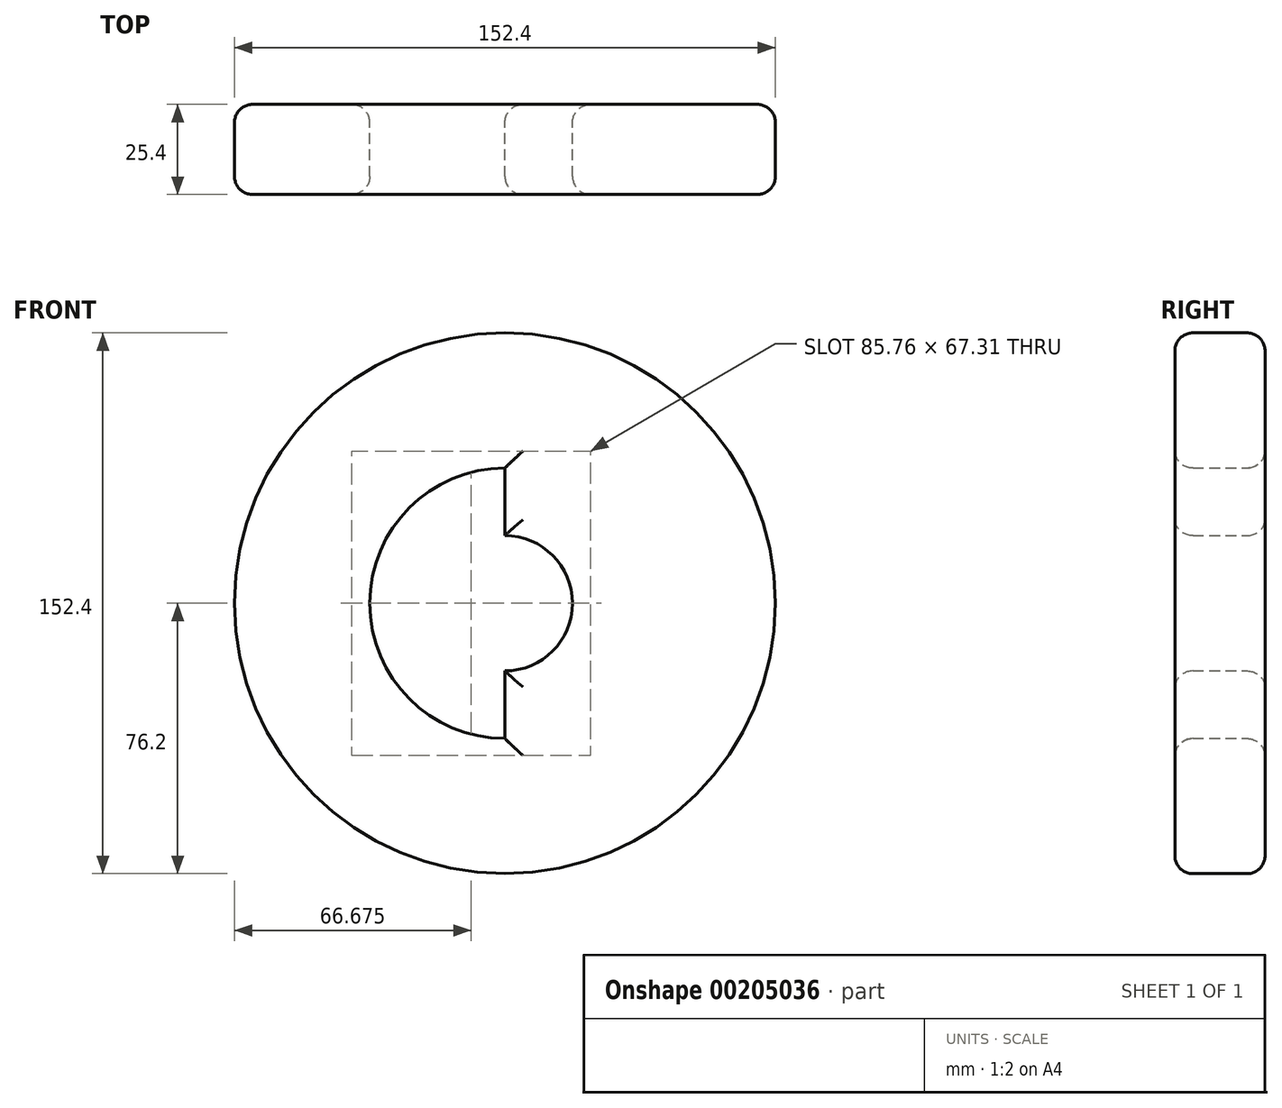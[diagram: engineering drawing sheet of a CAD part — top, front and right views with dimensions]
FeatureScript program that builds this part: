
annotation { "Feature Type Name" : "Feature", "Feature Type Description" : "" }
export const myFeature = defineFeature(function(context is Context, id is Id, definition is map)
    precondition{}
    {
        {
            var Q0;
            Q0=qCreatedBy(makeId("Front.planeOp"),FACE);
            var sketch = newSketch(context, id + "F0", { "sketchPlane" : qUnion([Q0])});
            skCircle(sketch, "E0", {"center": v(0, 0) * mm, "radius": 76.2 * mm});
            skLineSegment(sketch, "E1", {"start": v(-76.2, 0) * mm, "end": v(76.2, 0) * mm});
            skLineSegment(sketch, "E2", {"start": v(0, 76.2) * mm, "end": v(0, -76.2) * mm});
            skCircle(sketch, "E3", {"center": v(0, 0) * mm, "radius": 38.1 * mm});
            skSolve(sketch);
        }
        {
            var Q0;
            Q0=makeQuery(id+"F0.imprint","IMPRINT",FACE,{"disambiguationData":[TD([[makeQuery(id+"F0.imprint","IMPRINT",EDGE,{"derivedFrom":sQuery(id+"F0.wireOp",EDGE,"E0")}),1.0]])]});
            var Q1;
            {var subQ0=sQuery(id+"F0.wireOp",EDGE,"E3");var subQ1=sQuery(id+"F0.wireOp",EDGE,"E1");var subQ2=makeQuery(id+"F0.imprint","INTERSECT",VERTEX,{"disambiguationData":[OD(0.0)],"derivedFrom":[subQ1,subQ0]});Q1=makeQuery(id+"F0.imprint","IMPRINT",FACE,{"disambiguationData":[TD([[makeQuery(id+"F0.imprint","IMPRINT",EDGE,{"disambiguationData":[TD([[subQ2,-1.0]])],"derivedFrom":subQ1}),1.0]])]});}
            var Q2;
            {var subQ0=sQuery(id+"F0.wireOp",EDGE,"E3");var subQ1=sQuery(id+"F0.wireOp",EDGE,"E1");var subQ2=makeQuery(id+"F0.imprint","INTERSECT",VERTEX,{"disambiguationData":[OD(0.0)],"derivedFrom":[subQ1,subQ0]});Q2=makeQuery(id+"F0.imprint","IMPRINT",FACE,{"disambiguationData":[TD([[makeQuery(id+"F0.imprint","IMPRINT",EDGE,{"disambiguationData":[TD([[subQ2,-1.0]])],"derivedFrom":subQ1}),-1.0]])]});}
            var Q3;
            {var subQ0=sQuery(id+"F0.wireOp",EDGE,"E2");var subQ1=sQuery(id+"F0.wireOp",EDGE,"E1");var subQ2=makeQuery(id+"F0.imprint","INTERSECT",VERTEX,{"derivedFrom":[subQ1,subQ0]});Q3=makeQuery(id+"F0.imprint","IMPRINT",FACE,{"disambiguationData":[TD([[makeQuery(id+"F0.imprint","IMPRINT",EDGE,{"disambiguationData":[TD([[subQ2,-1.0]])],"derivedFrom":subQ1}),1.0]])]});}
            var Q4;
            {var subQ0=sQuery(id+"F0.wireOp",EDGE,"E2");var subQ1=sQuery(id+"F0.wireOp",EDGE,"E1");var subQ2=makeQuery(id+"F0.imprint","INTERSECT",VERTEX,{"derivedFrom":[subQ1,subQ0]});Q4=makeQuery(id+"F0.imprint","IMPRINT",FACE,{"disambiguationData":[TD([[makeQuery(id+"F0.imprint","IMPRINT",EDGE,{"disambiguationData":[TD([[subQ2,-1.0]])],"derivedFrom":subQ1}),-1.0]])]});}
            extrude(context, id + "F1", {"entities" : qUnion([Q0, Q1, Q2, Q3, Q4]), "depth" : 25.4 * mm});
        }
        {
            var Q0;
            Q0=sQuery(id+"F0.wireOp",VERTEX,"E3.center");
            var Q1;
            Q1=makeQuery(id+"F1.opExtrude","SWEPT_BODY",BODY,{"disambiguationData":[OSD([sQuery(id+"F0.wireOp",EDGE,"E0")])]});
            hole(context, id + "F2", {"style" : HoleStyle.SIMPLE, "endStyle" : HoleEndStyle.THROUGH, "oppositeDirection" : true, "holeDiameter" : 38.1 * mm, "locations" : qUnion([Q0]), "scope" : qUnion([Q1]), "isTappedThrough" : true});
        }
        {
            var Q0;
            Q0=makeQuery(id+"F1.opExtrude","CAP_FACE",FACE,{"disambiguationData":[OSD([sQuery(id+"F0.wireOp",EDGE,"E0")])],"isStart":false});
            var Q1;
            Q1=makeQuery(id+"F1.opExtrude","SWEPT_FACE",FACE,{"disambiguationData":[OSD([sQuery(id+"F0.wireOp",EDGE,"E0")])]});
            fillet(context, id + "F3", {"entities" : qUnion([Q0, Q1]), "radius" : 5.08 * mm, "tangentPropagation" : true, "allowEdgeOverflow" : false});
        }
        {
            var Q0;
            Q0=makeQuery(id+"F1.opExtrude","CAP_FACE",FACE,{"disambiguationData":[OSD([sQuery(id+"F0.wireOp",EDGE,"E0")])],"isStart":true});
            var Q1;
            Q1=makeQuery(id+"F2.hole-0.boolean.opBoolean","COPY",EDGE,{"derivedFrom":makeQuery(id+"F2.hole-0.opRevolve","SWEPT_EDGE",EDGE,{"disambiguationData":[OSD([sQuery(id+"F2.hole-0.sketch.wireOp",EDGE,"core_line_2"),sQuery(id+"F2.hole-0.sketch.wireOp",EDGE,"core_line_3")])]})});
            var Q2;
            {var subQ0=makeQuery(id+"F2.hole-0.opRevolve","SWEPT_FACE",FACE,{"disambiguationData":[OSD([sQuery(id+"F2.hole-0.sketch.wireOp",EDGE,"core_line_2")])]});Q2=makeQuery(id+"F3.opFillet","BLEND_EDGE",EDGE,{"blendedFrom":[makeQuery(id+"F2.hole-0.boolean.opBoolean","INTERSECT",EDGE,{"derivedFrom":[makeQuery(id+"F1.opExtrude","CAP_FACE",FACE,{"disambiguationData":[OSD([sQuery(id+"F0.wireOp",EDGE,"E0")])],"isStart":false}),subQ0]}),makeQuery(id+"F2.hole-0.boolean.opBoolean","COPY",FACE,{"derivedFrom":subQ0})],"blendedInto":[makeQuery(id+"F2.hole-0.boolean.opBoolean","COPY",FACE,{"derivedFrom":subQ0})]});}
            fillet(context, id + "F4", {"entities" : qUnion([Q0, Q1, Q2]), "radius" : 5.08 * mm, "tangentPropagation" : true, "allowEdgeOverflow" : false});
        }
    });
